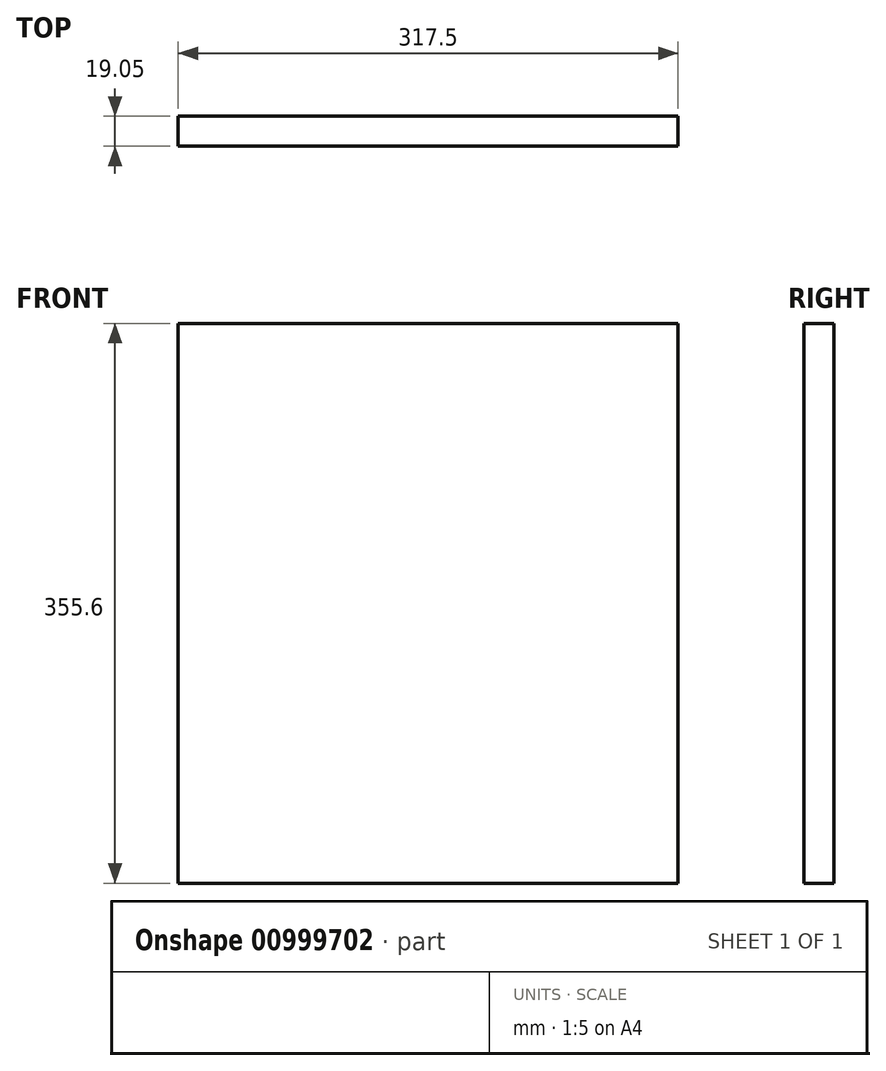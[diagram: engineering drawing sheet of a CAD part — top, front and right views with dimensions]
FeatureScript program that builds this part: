
annotation { "Feature Type Name" : "Feature", "Feature Type Description" : "" }
export const myFeature = defineFeature(function(context is Context, id is Id, definition is map)
    precondition{}
    {
        {
            var Q0;
            Q0=qCreatedBy(makeId("Front.planeOp"),FACE);
            var sketch = newSketch(context, id + "F0", { "sketchPlane" : qUnion([Q0])});
            skLineSegment(sketch, "E0.bottom", {"start": v(-158.75, -177.8) * mm, "end": v(158.75, -177.8) * mm});
            skLineSegment(sketch, "E0.top", {"start": v(-158.75, 177.8) * mm, "end": v(158.75, 177.8) * mm});
            skLineSegment(sketch, "E0.left", {"start": v(-158.75, -177.8) * mm, "end": v(-158.75, 177.8) * mm});
            skLineSegment(sketch, "E0.right", {"start": v(158.75, -177.8) * mm, "end": v(158.75, 177.8) * mm});
            skPoint(sketch, "E0.middle", {"position": v(0, 0) * mm});
            skSolve(sketch);
        }
        {
            var Q0;
            Q0 = qSketchRegion(id + "F0", true);
            extrude(context, id + "F1", {"entities" : qUnion([Q0]), "depth" : 19.05 * mm, "offsetDistance" : 25.4 * mm});
        }
    });
